# Revit family: ERA_LF_PC_SPP-402
name_source: partatom
category: Осветительные приборы
units: mm (PartAtom-declared; Revit-internal decimal feet)

## family parameters
Всегда вертикально = Да
Заголовок OmniClass = Lighting
Источник света = Да
На основе рабочей плоскости = Нет
Номер OmniClass = 23.80.70.00
Общий = Нет
При загрузке вырезать с полостями = Нет
Размер круглого соединителя = Использовать диаметр
Тип детали = Нормальный
Точка расчета площади = Да

## types (3) — shared parameters
ADSK_Единица измерения = шт.
ADSK_Завод-изготовитель = ЭРА
ADSK_Классификация нагрузок = Освещение
ADSK_Количество фаз = 1
ADSK_Коэффициент мощности = 0.95
ADSK_Наименование краткое = Светильник
ADSK_Напряжение = 230 В
ADSK_Примечание = Линейный драйвер, закалённое стекло
URL = https://www.eraworld.ru
_Корпус_Длина = 1 мм
_Корпус_Ширина = 1 мм
_Подвес_Диаметр = 1 мм
_Подвес_Расстояние = -49 мм
_Подвес_Чаша_Высота = 20 мм
_Подвес_Чаша_Диаметр = 10 мм
_УГО_Длина = 1 мм
_УГО_Ширина = 1 мм
Видимая форма излучения при визуализации = Нет
Высота чаши подвеса = 20 мм
Геометрия изделия = Круглый
Диаметр подвеса = 1 мм
Диаметр чаши подвеса = 10 мм
Излучение по длине прямоугольника = 1 мм
Излучение по ширине прямоугольника = 1 мм
Источник света = LED
Класс защиты = I
Класс пожароопасности = Нет
Комплект = Линейный драйвер
Разработчик модели = https://www.teslabim.ru
Светофильтр = 16777215
Смещение цветовой температуры при затухании лампы = <Нет>
Степень защиты IP = IP65
Тип установки = Подвесной
УГО_Масштаб = 100
Угол наклона = 90,00°
Файл фотометрической сетки = SPP-402-0-50K-100.ies
Цвет = Чёрный
zero-valued in all types: ADSK_Размер_Длина, ADSK_Размер_Ширина

## per-type parameters (varying)
| type | ADSK_Марка | ADSK_Масса | ADSK_Наименование | ADSK_Номинальная мощность | ADSK_Обозначение | ADSK_Полная мощность | ADSK_Размер_Высота | ADSK_Размер_Диаметр | _Корпус_Высота | _Корпус_Диаметр | _УГО_Диаметр |
| SPP-402-0-50K-100, LED, IP65, d 250х85 мм, 100 Вт, 5000 К, 10000 лм, класс защиты I, в комплекте (линейный драйвер) | SPP-402-0-50K-100 | 1.36 | Светильник, LED, круглый, подвесной, IP65, d 250х85 мм, 100 Вт, 5000 К, 10000 лм, класс защиты I, в комплекте (линейный драйвер) | 100 Вт | SPP-402-0-50K-100 | 105 В·А | 85 мм | 250 мм | 85 мм | 250 мм | 2.5 мм |
| SPP-402-0-50K-150, LED, IP65, d 298х88 мм, 150 Вт, 5000 К, 15000 лм, класс защиты I, в комплекте (линейный драйвер) | SPP-402-0-50K-150 | 2.1 | Светильник, LED, круглый, подвесной, IP65, d 298х88 мм, 150 Вт, 5000 К, 15000 лм, класс защиты I, в комплекте (линейный драйвер) | 150 Вт | SPP-402-0-50K-150 | 158 В·А | 88 мм | 298 мм | 88 мм | 298 мм | 2.98 мм |
| SPP-402-0-50K-200, LED, IP65, d 340х91 мм, 200 Вт, 5000 К, 20000 лм, класс защиты I, в комплекте (линейный драйвер) | SPP-402-0-50K-200 | 2.54 | Светильник, LED, круглый, подвесной, IP65, d 340х91 мм, 200 Вт, 5000 К, 20000 лм, класс защиты I, в комплекте (линейный драйвер) | 200 Вт | SPP-402-0-50K-200 | 211 В·А | 91 мм | 340 мм | 91 мм | 340 мм | 3.4 мм |
